# Revit family: Zaniboni-Diva-5_Inch_Aperture_40°-1
name_source: partatom
category: Lighting Fixtures
revit_build: Autodesk Revit 2016 (Build: 20150220_1215(x64)
units: mm (PartAtom-declared; Revit-internal decimal feet)

## family parameters
Cut with Voids When Loaded = No
Host = Face
Light Source = No
Part Type = Normal
Room Calculation Point = No
Round Connector Dimension = Use Diameter
Shared = No

## types (2) — shared parameters
Assembly Code = E1020300
Base Finish = ZBN - Metal Matte White
Beam = 36°
Body Finish = ZBN - Metal Matte White
CRI = 80
Default Elevation = 1"
Diffuser Finish = ZBN - Metal Matte White
Frame Finish = ZBN - Metal Matte White
Kelvin = 3000°K
Keynote = 12500
Manufacturer = Zaniboni
Mechanism Finish = ZBN - Plastic-Black
Screen Finish = ZBN - Glass
Support Finish = ZBN - Metal Matte White
Type Comments = Diva
URL = www.zanibonilighting.com
Voltage = 120 V
Wattage Comments = 14W
Width = 5 29/32"

## per-type parameters (varying)
| type | Description | Length | RD | RT | SD | ST |
| D4-D5TSN-0927A-2C-WS | 5 inch 1 Light Sources Adjustable 40° | 6" | No | No | No | No |
| D4-D5TTN2727A-2C-WS | 5 inch 3 Light Sources Adjustable 40° | 17 23/32" | Yes | Yes | Yes | Yes |

note: column(s) folded — value = type name in every type: Model

## geometry (parser evidence)
native form markers: Sweep x4
no freeform markers — native parametric forms only
